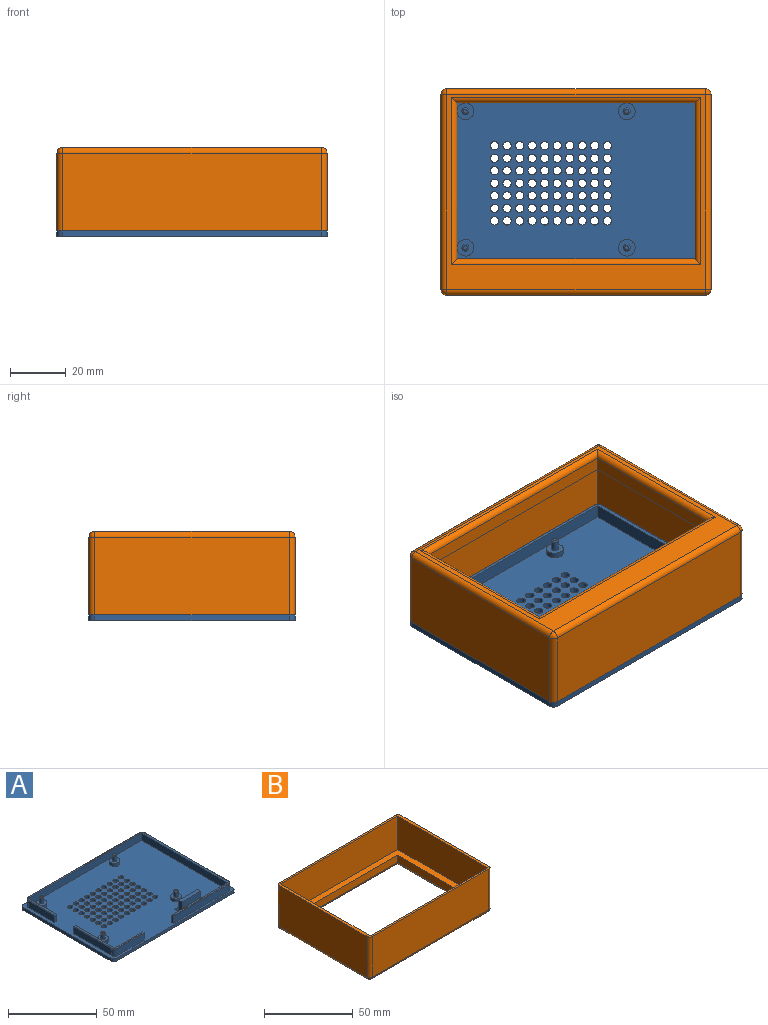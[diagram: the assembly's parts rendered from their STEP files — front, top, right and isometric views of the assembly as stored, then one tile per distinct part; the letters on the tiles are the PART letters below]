
ASSEMBLY  parts=2 mates=1
PART A: 144 faces, bbox 97x74x12 mm
  f0: plane 8.25x5mm, normal (0,1,0), area 41.2mm2, adj f1,f14,f17,f138
  f1: plane 97x74mm, normal (0,0,1), area 6087.3mm2, adj f0,f2,f3,f4,f5,f7,f8,f9
  f2: plane 70x2mm, normal (-1,0,0), area 140mm2, adj f1,f6,f61,f62
  f3: plane 93x2mm, normal (0,-1,0), area 186mm2, adj f1,f6,f59,f62
  f4: plane 70x2mm, normal (1,0,0), area 140mm2, adj f1,f6,f59,f60
  f5: plane 93x2mm, normal (0,1,0), area 186mm2, adj f1,f6,f60,f61
  f6: plane 97x74mm, normal (0,0,-1), area 6602.8mm2, adj f2,f3,f4,f5,f59,f60,f61,f62
  f7: plane 88x4.75mm, normal (0,1,0), area 418mm2, adj f1,f46,f48,f54
  f8: plane 20.75x4.75mm, normal (-1,0,0), area 98.6mm2, adj f1,f9,f48,f50
  f9: plane 5x1.5mm, normal (0,-1,0), area 7.5mm2, adj f1,f8,f10,f17,f50
  f10: plane 22x5mm, normal (1,0,0), area 110mm2, adj f1,f9,f11,f17
  f11: plane 90x5mm, normal (0,-1,0), area 450mm2, adj f1,f10,f12,f17
  f12: plane 68.5x5mm, normal (-1,0,0), area 342.5mm2, adj f1,f11,f13,f17
  f13: plane 21.5x5mm, normal (0,1,0), area 107.5mm2, adj f1,f12,f17,f140
  f14: plane 5x1.25mm, normal (-1,0,0), area 6.2mm2, adj f0,f1,f15,f17,f49
  f15: plane 43.75x4.75mm, normal (0,-1,0), area 207.8mm2, adj f1,f14,f47,f49
  f16: plane 66x4.75mm, normal (1,0,0), area 313.5mm2, adj f1,f46,f47,f53
  f17: plane 92.5x70.5mm, normal (0,0,1), area 240.9mm2, adj f0,f9,f10,f11,f12,f13,f14,f49
  f18: plane 30.25x4.75mm, normal (-1,0,0), area 143.7mm2, adj f1,f23,f45,f56
  f19: plane 21.25x4.75mm, normal (0,-1,0), area 100.9mm2, adj f1,f20,f45,f57
  f20: plane 5x1.25mm, normal (1,0,0), area 6.2mm2, adj f1,f19,f21,f24,f57
  f21: plane 22.25x5mm, normal (0,1,0), area 111.2mm2, adj f1,f20,f22,f24
  f22: plane 31.5x5mm, normal (1,0,0), area 157.5mm2, adj f1,f21,f23,f24
  f23: plane 5x1.5mm, normal (0,1,0), area 7.5mm2, adj f1,f18,f22,f24,f56
  f24: plane 32.5x23.5mm, normal (0,0,1), area 61.8mm2, adj f20,f21,f22,f23,f56,f57,f58
  f25: cylinder r=3mm len=6mm, axis (0,0,-1), area 37.7mm2, adj f1,f26
  f26: plane 6x6mm, normal (0,0,1), area 23.6mm2, adj f25,f33
  f27: cylinder r=3mm len=6mm, axis (0,0,-1), area 37.7mm2, adj f1,f28
  f28: plane 6x6mm, normal (0,0,1), area 23.6mm2, adj f27,f35
  f29: cylinder r=3mm len=6mm, axis (0,0,-1), area 37.7mm2, adj f1,f30
  f30: plane 6x6mm, normal (0,0,1), area 23.6mm2, adj f29,f37
  f31: cylinder r=3mm len=6mm, axis (0,0,-1), area 37.7mm2, adj f1,f32
  f32: plane 6x6mm, normal (0,0,1), area 23.6mm2, adj f31,f39
  f33: cylinder r=1.22mm len=3.5mm, axis (0,0,-1), area 26.9mm2, adj f26,f42
  f34: plane 1.45x1.45mm, normal (0,0,1), area 1.7mm2, adj f42
  f35: cylinder r=1.22mm len=3.5mm, axis (0,0,-1), area 26.9mm2, adj f28,f41
  f36: plane 1.45x1.45mm, normal (0,0,1), area 1.7mm2, adj f41
  f37: cylinder r=1.22mm len=3.5mm, axis (0,0,-1), area 26.9mm2, adj f30,f43
  f38: plane 1.45x1.45mm, normal (0,0,1), area 1.7mm2, adj f43
  f39: cylinder r=1.22mm len=3.5mm, axis (0,0,-1), area 26.9mm2, adj f32,f44
  f40: plane 1.45x1.45mm, normal (0,0,1), area 1.7mm2, adj f44
  f41: torus R=0.72mm, axis (0,0,1), area 5.1mm2, adj f35,f36
  f42: torus R=0.72mm, axis (0,0,1), area 5.1mm2, adj f33,f34
  f43: torus R=0.72mm, axis (0,0,1), area 5.1mm2, adj f37,f38
  f44: torus R=0.72mm, axis (0,0,1), area 5.1mm2, adj f39,f40
  f45: cylinder r=2.5mm len=4.75mm, axis (0,0,-1), area 18.7mm2, adj f1,f18,f19,f58
  f46: cylinder r=2.5mm len=4.75mm, axis (0,0,-1), area 18.7mm2, adj f1,f7,f16,f55
  f47: cylinder r=2.5mm len=4.75mm, axis (0,0,1), area 18.7mm2, adj f1,f15,f16,f51
  f48: cylinder r=2.5mm len=4.75mm, axis (0,0,1), area 18.7mm2, adj f1,f7,f8,f52
  f49: cylinder r=0.25mm len=43.75mm, axis (-1,0,0), area 17.2mm2, adj f14,f15,f17,f51
  f50: cylinder r=0.25mm len=20.75mm, axis (0,1,0), area 8.1mm2, adj f8,f9,f17,f52
  f51: torus R=2.25mm, axis (0,0,1), area 1.5mm2, adj f17,f47,f49,f53
  f52: torus R=2.25mm, axis (0,0,1), area 1.5mm2, adj f17,f48,f50,f54
  f53: cylinder r=0.25mm len=66mm, axis (0,-1,0), area 25.9mm2, adj f16,f17,f51,f55
  f54: cylinder r=0.25mm len=88mm, axis (1,0,0), area 34.6mm2, adj f7,f17,f52,f55
  f55: torus R=2.25mm, axis (0,0,1), area 1.5mm2, adj f17,f46,f53,f54
  f56: cylinder r=0.25mm len=30.25mm, axis (0,1,0), area 11.9mm2, adj f18,f23,f24,f58
  f57: cylinder r=0.25mm len=21.25mm, axis (-1,0,0), area 8.3mm2, adj f19,f20,f24,f58
  f58: torus R=2.25mm, axis (0,0,1), area 1.5mm2, adj f24,f45,f56,f57
  f59: cylinder r=2mm len=2mm, axis (0,0,-1), area 6.3mm2, adj f1,f3,f4,f6
  f60: cylinder r=2mm len=2mm, axis (0,0,1), area 6.3mm2, adj f1,f4,f5,f6
  f61: cylinder r=2mm len=2mm, axis (0,0,-1), area 6.3mm2, adj f1,f2,f5,f6
  f62: cylinder r=2mm len=2mm, axis (0,0,1), area 6.3mm2, adj f1,f2,f3,f6
  f63: cylinder r=1.5mm len=3mm, axis (0,0,-1), area 18.8mm2, adj f1,f6
  f64: cylinder r=1.5mm len=3mm, axis (0,0,-1), area 18.8mm2, adj f1,f6
  f65: cylinder r=1.5mm len=3mm, axis (0,0,-1), area 18.8mm2, adj f1,f6
  f66: cylinder r=1.5mm len=3mm, axis (0,0,-1), area 18.8mm2, adj f1,f6
  f67: cylinder r=1.5mm len=3mm, axis (0,0,-1), area 18.8mm2, adj f1,f6
  f68: cylinder r=1.5mm len=3mm, axis (0,0,-1), area 18.8mm2, adj f1,f6
  f69: cylinder r=1.5mm len=3mm, axis (0,0,-1), area 18.8mm2, adj f1,f6
  f70: cylinder r=1.5mm len=3mm, axis (0,0,-1), area 18.8mm2, adj f1,f6
  f71: cylinder r=1.5mm len=3mm, axis (0,0,-1), area 18.8mm2, adj f1,f6
  f72: cylinder r=1.5mm len=3mm, axis (0,0,-1), area 18.8mm2, adj f1,f6
  f73: cylinder r=1.5mm len=3mm, axis (0,0,-1), area 18.8mm2, adj f1,f6
  f74: cylinder r=1.5mm len=3mm, axis (0,0,-1), area 18.8mm2, adj f1,f6
  f75: cylinder r=1.5mm len=3mm, axis (0,0,-1), area 18.8mm2, adj f1,f6
  f76: cylinder r=1.5mm len=3mm, axis (0,0,-1), area 18.8mm2, adj f1,f6
  f77: cylinder r=1.5mm len=3mm, axis (0,0,-1), area 18.8mm2, adj f1,f6
  f78: cylinder r=1.5mm len=3mm, axis (0,0,-1), area 18.8mm2, adj f1,f6
  f79: cylinder r=1.5mm len=3mm, axis (0,0,-1), area 18.8mm2, adj f1,f6
  f80: cylinder r=1.5mm len=3mm, axis (0,0,-1), area 18.8mm2, adj f1,f6
  f81: cylinder r=1.5mm len=3mm, axis (0,0,-1), area 18.8mm2, adj f1,f6
  f82: cylinder r=1.5mm len=3mm, axis (0,0,-1), area 18.8mm2, adj f1,f6
  f83: cylinder r=1.5mm len=3mm, axis (0,0,-1), area 18.8mm2, adj f1,f6
  f84: cylinder r=1.5mm len=3mm, axis (0,0,-1), area 18.8mm2, adj f1,f6
  f85: cylinder r=1.5mm len=3mm, axis (0,0,-1), area 18.8mm2, adj f1,f6
  f86: cylinder r=1.5mm len=3mm, axis (0,0,-1), area 18.8mm2, adj f1,f6
  f87: cylinder r=1.5mm len=3mm, axis (0,0,-1), area 18.8mm2, adj f1,f6
  f88: cylinder r=1.5mm len=3mm, axis (0,0,-1), area 18.8mm2, adj f1,f6
  f89: cylinder r=1.5mm len=3mm, axis (0,0,-1), area 18.8mm2, adj f1,f6
  f90: cylinder r=1.5mm len=3mm, axis (0,0,-1), area 18.8mm2, adj f1,f6
  f91: cylinder r=1.5mm len=3mm, axis (0,0,-1), area 18.8mm2, adj f1,f6
  f92: cylinder r=1.5mm len=3mm, axis (0,0,-1), area 18.8mm2, adj f1,f6
  f93: cylinder r=1.5mm len=3mm, axis (0,0,-1), area 18.8mm2, adj f1,f6
  f94: cylinder r=1.5mm len=3mm, axis (0,0,-1), area 18.8mm2, adj f1,f6
  f95: cylinder r=1.5mm len=3mm, axis (0,0,-1), area 18.8mm2, adj f1,f6
  f96: cylinder r=1.5mm len=3mm, axis (0,0,-1), area 18.8mm2, adj f1,f6
  f97: cylinder r=1.5mm len=3mm, axis (0,0,-1), area 18.8mm2, adj f1,f6
  f98: cylinder r=1.5mm len=3mm, axis (0,0,-1), area 18.8mm2, adj f1,f6
  f99: cylinder r=1.5mm len=3mm, axis (0,0,-1), area 18.8mm2, adj f1,f6
  f100: cylinder r=1.5mm len=3mm, axis (0,0,-1), area 18.8mm2, adj f1,f6
  f101: cylinder r=1.5mm len=3mm, axis (0,0,-1), area 18.8mm2, adj f1,f6
  f102: cylinder r=1.5mm len=3mm, axis (0,0,-1), area 18.8mm2, adj f1,f6
  f103: cylinder r=1.5mm len=3mm, axis (0,0,-1), area 18.8mm2, adj f1,f6
  f104: cylinder r=1.5mm len=3mm, axis (0,0,-1), area 18.8mm2, adj f1,f6
  f105: cylinder r=1.5mm len=3mm, axis (0,0,-1), area 18.8mm2, adj f1,f6
  f106: cylinder r=1.5mm len=3mm, axis (0,0,-1), area 18.8mm2, adj f1,f6
  f107: cylinder r=1.5mm len=3mm, axis (0,0,-1), area 18.8mm2, adj f1,f6
  f108: cylinder r=1.5mm len=3mm, axis (0,0,-1), area 18.8mm2, adj f1,f6
  f109: cylinder r=1.5mm len=3mm, axis (0,0,-1), area 18.8mm2, adj f1,f6
  f110: cylinder r=1.5mm len=3mm, axis (0,0,-1), area 18.8mm2, adj f1,f6
  f111: cylinder r=1.5mm len=3mm, axis (0,0,-1), area 18.8mm2, adj f1,f6
  f112: cylinder r=1.5mm len=3mm, axis (0,0,-1), area 18.8mm2, adj f1,f6
  f113: cylinder r=1.5mm len=3mm, axis (0,0,-1), area 18.8mm2, adj f1,f6
  f114: cylinder r=1.5mm len=3mm, axis (0,0,-1), area 18.8mm2, adj f1,f6
  f115: cylinder r=1.5mm len=3mm, axis (0,0,-1), area 18.8mm2, adj f1,f6
  f116: cylinder r=1.5mm len=3mm, axis (0,0,-1), area 18.8mm2, adj f1,f6
  f117: cylinder r=1.5mm len=3mm, axis (0,0,-1), area 18.8mm2, adj f1,f6
  f118: cylinder r=1.5mm len=3mm, axis (0,0,-1), area 18.8mm2, adj f1,f6
  f119: cylinder r=1.5mm len=3mm, axis (0,0,-1), area 18.8mm2, adj f1,f6
  f120: cylinder r=1.5mm len=3mm, axis (0,0,-1), area 18.8mm2, adj f1,f6
  f121: cylinder r=1.5mm len=3mm, axis (0,0,-1), area 18.8mm2, adj f1,f6
  f122: cylinder r=1.5mm len=3mm, axis (0,0,-1), area 18.8mm2, adj f1,f6
  f123: cylinder r=1.5mm len=3mm, axis (0,0,-1), area 18.8mm2, adj f1,f6
  f124: cylinder r=1.5mm len=3mm, axis (0,0,-1), area 18.8mm2, adj f1,f6
  f125: cylinder r=1.5mm len=3mm, axis (0,0,-1), area 18.8mm2, adj f1,f6
  f126: cylinder r=1.5mm len=3mm, axis (0,0,-1), area 18.8mm2, adj f1,f6
  f127: cylinder r=1.5mm len=3mm, axis (0,0,-1), area 18.8mm2, adj f1,f6
  f128: cylinder r=1.5mm len=3mm, axis (0,0,-1), area 18.8mm2, adj f1,f6
  f129: cylinder r=1.5mm len=3mm, axis (0,0,-1), area 18.8mm2, adj f1,f6
  f130: cylinder r=1.5mm len=3mm, axis (0,0,-1), area 18.8mm2, adj f1,f6
  f131: cylinder r=1.5mm len=3mm, axis (0,0,-1), area 18.8mm2, adj f1,f6
  f132: cylinder r=1.5mm len=3mm, axis (0,0,-1), area 18.8mm2, adj f1,f6
  f133: plane 7x2mm, normal (1,0,0), area 14mm2, adj f1,f6,f134,f136,f142
  f134: plane 11x2mm, normal (0,1,0), area 22mm2, adj f6,f133,f135,f142
  f135: plane 7x2mm, normal (-1,0,0), area 14mm2, adj f1,f6,f134,f136,f142
  f136: plane 11x2mm, normal (0,-1,0), area 22mm2, adj f1,f6,f133,f135
  f137: plane 15x10mm, normal (0,1,0), area 150mm2, adj f1,f138,f140,f141,f142
  f138: plane 10x3mm, normal (-1,0,0), area 25.1mm2, adj f0,f1,f17,f137,f139,f141,f143
  f139: plane 15x4.5mm, normal (0,-1,0), area 67.5mm2, adj f138,f140,f141,f143
  f140: plane 10x3mm, normal (1,0,0), area 25.1mm2, adj f1,f13,f17,f137,f139,f141,f143
  f141: plane 15x2.5mm, normal (0,0,1), area 37.5mm2, adj f137,f138,f139,f140
  f142: plane 11x1.5mm, normal (0,0,-1), area 16.5mm2, adj f133,f134,f135,f137
  f143: cylinder r=0.5mm len=15mm, axis (-1,0,0), area 11.8mm2, adj f17,f138,f139,f140
PART B: 31 faces, bbox 97x74x30 mm
  f0: plane 56x5mm, normal (-1,0,0), area 280mm2, adj f1,f7,f8,f27
  f1: plane 85.5x5mm, normal (0,1,0), area 427.5mm2, adj f0,f2,f8,f29
  f2: plane 56x5mm, normal (1,0,0), area 280mm2, adj f1,f7,f8,f30
  f3: plane 70x28mm, normal (-1,0,0), area 1960mm2, adj f14,f20,f24,f26
  f4: plane 93x28mm, normal (0,-1,0), area 2604mm2, adj f14,f17,f23,f26
  f5: plane 70x28mm, normal (1,0,0), area 1960mm2, adj f14,f15,f17,f18
  f6: plane 93x28mm, normal (0,1,0), area 2604mm2, adj f14,f15,f19,f20
  f7: plane 85.5x5mm, normal (0,-1,0), area 427.5mm2, adj f0,f2,f8,f28
  f8: plane 93.5x71.5mm, normal (0,0,1), area 1897.2mm2, adj f0,f1,f2,f7,f10,f11,f12,f13
  f9: plane 93x70mm, normal (0,0,-1), area 1140mm2, adj f18,f19,f23,f24,f27,f28,f29,f30
  f10: plane 93.5x23mm, normal (0,1,0), area 2150.5mm2, adj f8,f11,f13,f14
  f11: plane 71.5x23mm, normal (1,0,0), area 1644.5mm2, adj f8,f10,f12,f14
  f12: plane 93.5x23mm, normal (0,-1,0), area 2150.5mm2, adj f8,f11,f13,f14
  f13: plane 71.5x23mm, normal (-1,0,0), area 1644.5mm2, adj f8,f10,f12,f14
  f14: plane 97x74mm, normal (0,0,1), area 489.3mm2, adj f3,f4,f5,f6,f10,f11,f12,f13
  f15: cylinder r=2mm len=28mm, axis (0,0,1), area 88mm2, adj f5,f6,f14,f16
  f16: sphere r=2mm, area 6.3mm2, adj f15,f18,f19
  f17: cylinder r=2mm len=28mm, axis (0,0,-1), area 88mm2, adj f4,f5,f14,f21
  f18: cylinder r=2mm len=70mm, axis (0,1,0), area 219.9mm2, adj f5,f9,f16,f21
  f19: cylinder r=2mm len=93mm, axis (-1,0,0), area 292.2mm2, adj f6,f9,f16,f22
  f20: cylinder r=2mm len=28mm, axis (0,0,-1), area 88mm2, adj f3,f6,f14,f22
  f21: sphere r=2mm, area 6.3mm2, adj f17,f18,f23
  f22: sphere r=2mm, area 6.3mm2, adj f19,f20,f24
  f23: cylinder r=2mm len=93mm, axis (1,0,0), area 292.2mm2, adj f4,f9,f21,f25
  f24: cylinder r=2mm len=70mm, axis (0,-1,0), area 219.9mm2, adj f3,f9,f22,f25
  f25: sphere r=2mm, area 6.3mm2, adj f23,f24,f26
  f26: cylinder r=2mm len=28mm, axis (0,0,1), area 88mm2, adj f3,f4,f14,f25
  f27: cylinder r=2mm len=60mm, axis (0,-1,0), area 180.5mm2, adj f0,f9,f28,f29
  f28: cylinder r=2mm len=89.5mm, axis (1,0,0), area 273.2mm2, adj f7,f9,f27,f30
  f29: cylinder r=2mm len=89.5mm, axis (-1,0,0), area 273.2mm2, adj f1,f9,f27,f30
  f30: cylinder r=2mm len=60mm, axis (0,1,0), area 180.5mm2, adj f2,f9,f28,f29
PLACE A rot(axis=(1,0,0),0deg) t=(-12.9,-9.16,-10.33)mm
PLACE B rot(axis=(0,1,0),180deg) t=(84.1,-9.16,21.67)mm
MATE fastened A.f1 <-> B.f14  axis (0,0,1) through (35.6,-9.16,-8.33)mm
